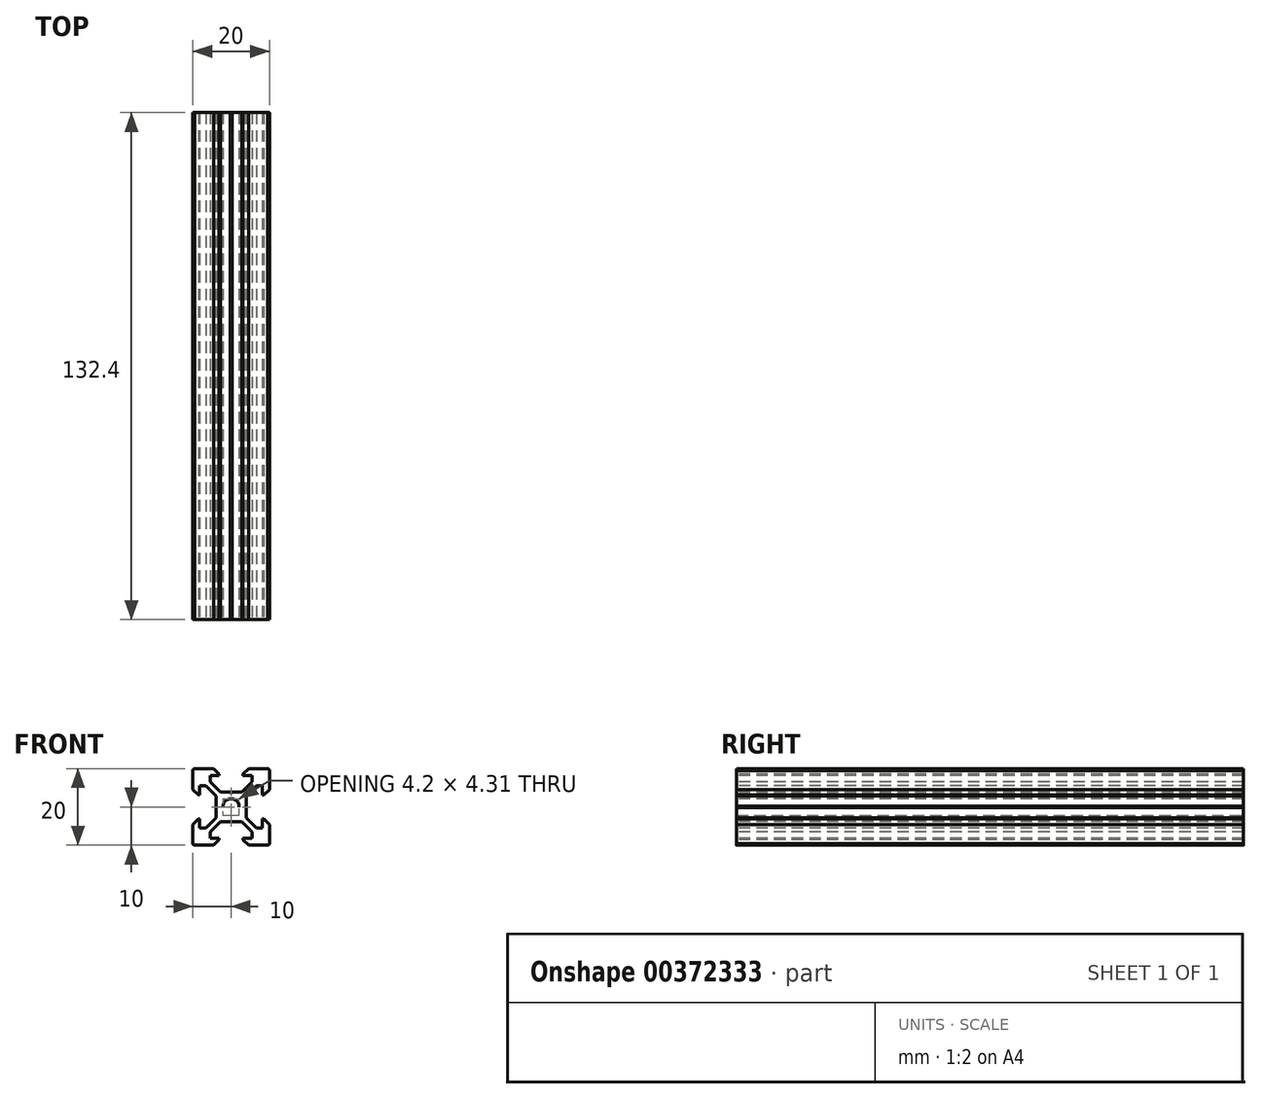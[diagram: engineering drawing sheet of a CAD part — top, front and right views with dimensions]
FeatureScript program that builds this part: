
annotation { "Feature Type Name" : "Feature", "Feature Type Description" : "" }
export const myFeature = defineFeature(function(context is Context, id is Id, definition is map)
    precondition{}
    {
        {
            var Q0;
            Q0=qCreatedBy(makeId("Front.planeOp"),FACE);
            var sketch = newSketch(context, id + "F0", { "sketchPlane" : qUnion([Q0])});
            skFitSpline(sketch, "E0.0", {"points": [v(-8.2, 3.13) * mm, v(-8.2, 3.92) * mm, v(-8.2, 4.7) * mm, v(-8.2, 5.5) * mm]});
            skFitSpline(sketch, "E0.1", {"points": [v(-8.2, 5.5) * mm, v(-7.65, 5.5) * mm, v(-7.1, 5.5) * mm, v(-6.56, 5.5) * mm]});
            skFitSpline(sketch, "E0.2", {"points": [v(-6.56, 5.5) * mm, v(-5.67, 4.61) * mm, v(-4.79, 3.73) * mm, v(-3.9, 2.84) * mm]});
            skFitSpline(sketch, "E0.3", {"points": [v(-2.84, 3.9) * mm, v(-3.73, 4.79) * mm, v(-4.61, 5.67) * mm, v(-5.5, 6.56) * mm]});
            skFitSpline(sketch, "E0.4", {"points": [v(-5.5, 6.56) * mm, v(-5.5, 7.1) * mm, v(-5.5, 7.65) * mm, v(-5.5, 8.2) * mm]});
            skFitSpline(sketch, "E0.5", {"points": [v(-5.5, 8.2) * mm, v(-4.7, 8.2) * mm, v(-3.92, 8.2) * mm, v(-3.12, 8.2) * mm]});
            skFitSpline(sketch, "E0.6", {"points": [v(-3.12, 8.2) * mm, v(-3.12, 8.32) * mm, v(-3.12, 8.43) * mm, v(-3.12, 8.55) * mm]});
            skFitSpline(sketch, "E0.7", {"points": [v(-10, 4.58) * mm, v(-9.51, 4.1) * mm, v(-9.03, 3.61) * mm, v(-8.54, 3.13) * mm]});
            skFitSpline(sketch, "E0.8", {"points": [v(-8.54, 3.13) * mm, v(-8.43, 3.13) * mm, v(-8.31, 3.13) * mm, v(-8.2, 3.13) * mm]});
            skFitSpline(sketch, "E0.9", {"points": [v(-10, 9.5) * mm, v(-10, 7.86) * mm, v(-10, 6.22) * mm, v(-10, 4.58) * mm]});
            skFitSpline(sketch, "E0.10", {"points": [v(-9.5, 10) * mm, v(-9.57, 10) * mm, v(-9.63, 9.99) * mm, v(-9.7, 9.96) * mm, v(-9.75, 9.94) * mm, v(-9.8, 9.9) * mm, v(-9.85, 9.85) * mm, v(-9.9, 9.8) * mm, v(-9.94, 9.75) * mm, v(-9.96, 9.7) * mm, v(-9.99, 9.63) * mm, v(-10, 9.57) * mm, v(-10, 9.5) * mm]});
            skFitSpline(sketch, "E0.11", {"points": [v(-4.58, 10) * mm, v(-6.22, 10) * mm, v(-7.86, 10) * mm, v(-9.5, 10) * mm]});
            skFitSpline(sketch, "E0.12", {"points": [v(-3.9, 2.84) * mm, v(-3.9, 1.96) * mm, v(-3.9, 1.09) * mm, v(-3.9, 0.21) * mm]});
            skFitSpline(sketch, "E0.13", {"points": [v(-3.9, 0.21) * mm, v(-3.83, 0.14) * mm, v(-3.76, 0.07) * mm, v(-3.69, 0) * mm]});
            skFitSpline(sketch, "E0.14", {"points": [v(-0.2, 3.9) * mm, v(-1.09, 3.9) * mm, v(-1.96, 3.9) * mm, v(-2.84, 3.9) * mm]});
            skFitSpline(sketch, "E0.15", {"points": [v(0, 3.7) * mm, v(-0.07, 3.76) * mm, v(-0.14, 3.83) * mm, v(-0.2, 3.9) * mm]});
            skFitSpline(sketch, "E0.16", {"points": [v(2.1, 0) * mm, v(2.1, 0.27) * mm, v(2, 0.82) * mm, v(1.52, 1.52) * mm, v(0.82, 2) * mm, v(0, 2.15) * mm, v(-0.82, 2) * mm, v(-1.52, 1.52) * mm, v(-2, 0.82) * mm, v(-2.1, 0.27) * mm, v(-2.1, 0) * mm]});
            skFitSpline(sketch, "E1.0", {"points": [v(-8.2, 3.13) * mm, v(-8.2, 3.92) * mm, v(-8.2, 4.7) * mm, v(-8.2, 5.5) * mm]});
            skFitSpline(sketch, "E1.1", {"points": [v(-8.2, 5.5) * mm, v(-7.65, 5.5) * mm, v(-7.1, 5.5) * mm, v(-6.56, 5.5) * mm]});
            skFitSpline(sketch, "E1.2", {"points": [v(-6.56, 5.5) * mm, v(-5.67, 4.61) * mm, v(-4.79, 3.73) * mm, v(-3.9, 2.84) * mm]});
            skFitSpline(sketch, "E1.3", {"points": [v(-2.84, 3.9) * mm, v(-3.73, 4.79) * mm, v(-4.61, 5.67) * mm, v(-5.5, 6.56) * mm]});
            skFitSpline(sketch, "E1.4", {"points": [v(-5.5, 6.56) * mm, v(-5.5, 7.1) * mm, v(-5.5, 7.65) * mm, v(-5.5, 8.2) * mm]});
            skFitSpline(sketch, "E1.5", {"points": [v(-5.5, 8.2) * mm, v(-4.7, 8.2) * mm, v(-3.92, 8.2) * mm, v(-3.12, 8.2) * mm]});
            skFitSpline(sketch, "E1.6", {"points": [v(-3.12, 8.2) * mm, v(-3.12, 8.32) * mm, v(-3.12, 8.43) * mm, v(-3.12, 8.55) * mm]});
            skFitSpline(sketch, "E1.7", {"points": [v(-10, 4.58) * mm, v(-9.51, 4.1) * mm, v(-9.03, 3.61) * mm, v(-8.54, 3.13) * mm]});
            skFitSpline(sketch, "E1.8", {"points": [v(-8.54, 3.13) * mm, v(-8.43, 3.13) * mm, v(-8.31, 3.13) * mm, v(-8.2, 3.13) * mm]});
            skFitSpline(sketch, "E1.9", {"points": [v(-10, 9.5) * mm, v(-10, 7.86) * mm, v(-10, 6.22) * mm, v(-10, 4.58) * mm]});
            skFitSpline(sketch, "E1.10", {"points": [v(-9.5, 10) * mm, v(-9.57, 10) * mm, v(-9.63, 9.99) * mm, v(-9.7, 9.96) * mm, v(-9.75, 9.94) * mm, v(-9.8, 9.9) * mm, v(-9.85, 9.85) * mm, v(-9.9, 9.8) * mm, v(-9.94, 9.75) * mm, v(-9.96, 9.7) * mm, v(-9.99, 9.63) * mm, v(-10, 9.57) * mm, v(-10, 9.5) * mm]});
            skFitSpline(sketch, "E1.11", {"points": [v(-4.58, 10) * mm, v(-6.22, 10) * mm, v(-7.86, 10) * mm, v(-9.5, 10) * mm]});
            skFitSpline(sketch, "E1.12", {"points": [v(-3.9, 2.84) * mm, v(-3.9, 1.96) * mm, v(-3.9, 1.09) * mm, v(-3.9, 0.21) * mm]});
            skFitSpline(sketch, "E1.13", {"points": [v(-3.9, 0.21) * mm, v(-3.83, 0.14) * mm, v(-3.76, 0.07) * mm, v(-3.69, 0) * mm]});
            skFitSpline(sketch, "E1.14", {"points": [v(-0.2, 3.9) * mm, v(-1.09, 3.9) * mm, v(-1.96, 3.9) * mm, v(-2.84, 3.9) * mm]});
            skFitSpline(sketch, "E1.15", {"points": [v(0, 3.7) * mm, v(-0.07, 3.76) * mm, v(-0.14, 3.83) * mm, v(-0.2, 3.9) * mm]});
            skFitSpline(sketch, "E1.16", {"points": [v(2.1, 0) * mm, v(2.1, 0.27) * mm, v(2, 0.82) * mm, v(1.52, 1.52) * mm, v(0.82, 2) * mm, v(0, 2.15) * mm, v(-0.82, 2) * mm, v(-1.52, 1.52) * mm, v(-2, 0.82) * mm, v(-2.1, 0.27) * mm, v(-2.1, 0) * mm]});
            skFitSpline(sketch, "E2.0", {"points": [v(2.84, 3.9) * mm, v(1.96, 3.9) * mm, v(1.09, 3.9) * mm, v(0.21, 3.9) * mm]});
            skFitSpline(sketch, "E2.1", {"points": [v(0.21, 3.9) * mm, v(0.14, 3.83) * mm, v(0.07, 3.76) * mm, v(0, 3.7) * mm]});
            skFitSpline(sketch, "E2.2", {"points": [v(3.9, 0.2) * mm, v(3.9, 1.09) * mm, v(3.9, 1.96) * mm, v(3.9, 2.84) * mm]});
            skFitSpline(sketch, "E2.3", {"points": [v(3.69, 0) * mm, v(3.76, 0.07) * mm, v(3.83, 0.14) * mm, v(3.9, 0.2) * mm]});
            skFitSpline(sketch, "E2.4", {"points": [v(3.9, 2.84) * mm, v(4.79, 3.73) * mm, v(5.67, 4.61) * mm, v(6.56, 5.5) * mm]});
            skFitSpline(sketch, "E2.5", {"points": [v(5.5, 6.56) * mm, v(4.61, 5.67) * mm, v(3.73, 4.79) * mm, v(2.84, 3.9) * mm]});
            skFitSpline(sketch, "E2.6", {"points": [v(6.56, 5.5) * mm, v(7.1, 5.5) * mm, v(7.65, 5.5) * mm, v(8.2, 5.5) * mm]});
            skFitSpline(sketch, "E2.7", {"points": [v(8.2, 5.5) * mm, v(8.2, 4.7) * mm, v(8.2, 3.92) * mm, v(8.2, 3.13) * mm]});
            skFitSpline(sketch, "E2.8", {"points": [v(8.2, 3.13) * mm, v(8.31, 3.13) * mm, v(8.43, 3.13) * mm, v(8.54, 3.13) * mm]});
            skFitSpline(sketch, "E2.9", {"points": [v(8.54, 3.13) * mm, v(9.03, 3.61) * mm, v(9.51, 4.1) * mm, v(10, 4.58) * mm]});
            skFitSpline(sketch, "E2.10", {"points": [v(10, 4.58) * mm, v(10, 6.22) * mm, v(10, 7.86) * mm, v(10, 9.5) * mm]});
            skFitSpline(sketch, "E2.11", {"points": [v(5.5, 8.2) * mm, v(5.5, 7.65) * mm, v(5.5, 7.1) * mm, v(5.5, 6.56) * mm]});
            skFitSpline(sketch, "E2.12", {"points": [v(3.13, 8.2) * mm, v(3.92, 8.2) * mm, v(4.7, 8.2) * mm, v(5.5, 8.2) * mm]});
            skFitSpline(sketch, "E2.13", {"points": [v(3.13, 8.55) * mm, v(3.13, 8.43) * mm, v(3.13, 8.32) * mm, v(3.13, 8.2) * mm]});
            skFitSpline(sketch, "E2.14", {"points": [v(9.5, 10) * mm, v(7.86, 10) * mm, v(6.22, 10) * mm, v(4.58, 10) * mm]});
            skFitSpline(sketch, "E2.15", {"points": [v(10, 9.5) * mm, v(10, 9.57) * mm, v(9.99, 9.63) * mm, v(9.96, 9.7) * mm, v(9.94, 9.75) * mm, v(9.9, 9.8) * mm, v(9.85, 9.85) * mm, v(9.8, 9.9) * mm, v(9.75, 9.94) * mm, v(9.7, 9.96) * mm, v(9.63, 9.99) * mm, v(9.57, 10) * mm, v(9.5, 10) * mm]});
            skFitSpline(sketch, "E2.16", {"points": [v(4.58, 10) * mm, v(4.1, 9.52) * mm, v(3.61, 9.03) * mm, v(3.13, 8.55) * mm]});
            skLineSegment(sketch, "E3", {"start": v(-4.58, 10) * mm, "end": v(-3.12, 8.55) * mm});
            skFitSpline(sketch, "E4.MirrorCS", {"points": [v(-3.9, -0.2) * mm, v(-3.83, -0.14) * mm, v(-3.76, -0.07) * mm, v(-3.69, 0) * mm]});
            skFitSpline(sketch, "E5.MirrorCS", {"points": [v(0, -3.7) * mm, v(-0.07, -3.76) * mm, v(-0.14, -3.83) * mm, v(-0.21, -3.9) * mm]});
            skFitSpline(sketch, "E6.MirrorCS", {"points": [v(-8.55, -3.12) * mm, v(-8.43, -3.12) * mm, v(-8.32, -3.12) * mm, v(-8.2, -3.12) * mm]});
            skFitSpline(sketch, "E7.MirrorCS", {"points": [v(0.2, -3.9) * mm, v(0.14, -3.83) * mm, v(0.07, -3.76) * mm, v(0, -3.7) * mm]});
            skFitSpline(sketch, "E8.MirrorCS", {"points": [v(-3.13, -8.2) * mm, v(-3.13, -8.31) * mm, v(-3.13, -8.43) * mm, v(-3.13, -8.54) * mm]});
            skFitSpline(sketch, "E9.MirrorCS", {"points": [v(-3.9, -0.2) * mm, v(-3.83, -0.14) * mm, v(-3.76, -0.07) * mm, v(-3.69, 0) * mm]});
            skFitSpline(sketch, "E10.MirrorCS", {"points": [v(-8.55, -3.12) * mm, v(-8.43, -3.12) * mm, v(-8.32, -3.12) * mm, v(-8.2, -3.12) * mm]});
            skFitSpline(sketch, "E11.MirrorCS", {"points": [v(0, -3.7) * mm, v(-0.07, -3.76) * mm, v(-0.14, -3.83) * mm, v(-0.21, -3.9) * mm]});
            skFitSpline(sketch, "E12.MirrorCS", {"points": [v(-3.13, -8.2) * mm, v(-3.13, -8.31) * mm, v(-3.13, -8.43) * mm, v(-3.13, -8.54) * mm]});
            skFitSpline(sketch, "E13.MirrorCS", {"points": [v(3.12, -8.55) * mm, v(3.12, -8.43) * mm, v(3.12, -8.32) * mm, v(3.12, -8.2) * mm]});
            skFitSpline(sketch, "E14.MirrorCS", {"points": [v(3.69, 0) * mm, v(3.76, -0.07) * mm, v(3.83, -0.14) * mm, v(3.9, -0.21) * mm]});
            skFitSpline(sketch, "E15.MirrorCS", {"points": [v(8.2, -3.13) * mm, v(8.31, -3.13) * mm, v(8.43, -3.13) * mm, v(8.54, -3.13) * mm]});
            skFitSpline(sketch, "E16.MirrorCS", {"points": [v(-8.2, -5.5) * mm, v(-7.65, -5.5) * mm, v(-7.1, -5.5) * mm, v(-6.56, -5.5) * mm]});
            skFitSpline(sketch, "E17.MirrorCS", {"points": [v(-2.84, -3.9) * mm, v(-3.73, -4.79) * mm, v(-4.61, -5.67) * mm, v(-5.5, -6.56) * mm]});
            skFitSpline(sketch, "E18.MirrorCS", {"points": [v(-5.5, -8.2) * mm, v(-4.7, -8.2) * mm, v(-3.92, -8.2) * mm, v(-3.13, -8.2) * mm]});
            skFitSpline(sketch, "E19.MirrorCS", {"points": [v(-5.5, -6.56) * mm, v(-5.5, -7.1) * mm, v(-5.5, -7.65) * mm, v(-5.5, -8.2) * mm]});
            skFitSpline(sketch, "E20.MirrorCS", {"points": [v(-0.21, -3.9) * mm, v(-1.09, -3.9) * mm, v(-1.96, -3.9) * mm, v(-2.84, -3.9) * mm]});
            skFitSpline(sketch, "E21.MirrorCS", {"points": [v(-8.2, -3.12) * mm, v(-8.2, -3.92) * mm, v(-8.2, -4.7) * mm, v(-8.2, -5.5) * mm]});
            skFitSpline(sketch, "E22.MirrorCS", {"points": [v(-10, -4.58) * mm, v(-9.52, -4.1) * mm, v(-9.03, -3.6) * mm, v(-8.55, -3.12) * mm]});
            skFitSpline(sketch, "E23.MirrorCS", {"points": [v(-10, -9.5) * mm, v(-10, -7.86) * mm, v(-10, -6.22) * mm, v(-10, -4.58) * mm]});
            skFitSpline(sketch, "E24.MirrorCS", {"points": [v(-9.5, -10) * mm, v(-9.57, -10) * mm, v(-9.63, -9.99) * mm, v(-9.7, -9.96) * mm, v(-9.75, -9.94) * mm, v(-9.8, -9.9) * mm, v(-9.85, -9.85) * mm, v(-9.9, -9.8) * mm, v(-9.94, -9.75) * mm, v(-9.96, -9.7) * mm, v(-9.99, -9.63) * mm, v(-10, -9.57) * mm, v(-10, -9.5) * mm]});
            skFitSpline(sketch, "E25.MirrorCS", {"points": [v(-4.58, -10) * mm, v(-6.22, -10) * mm, v(-7.86, -10) * mm, v(-9.5, -10) * mm]});
            skFitSpline(sketch, "E26.MirrorCS", {"points": [v(-3.9, -2.84) * mm, v(-3.9, -1.96) * mm, v(-3.9, -1.09) * mm, v(-3.9, -0.21) * mm]});
            skFitSpline(sketch, "E27.MirrorCS", {"points": [v(-6.56, -5.5) * mm, v(-5.67, -4.61) * mm, v(-4.79, -3.73) * mm, v(-3.9, -2.84) * mm]});
            skFitSpline(sketch, "E28.MirrorCS", {"points": [v(2.1, 0) * mm, v(2.1, -0.27) * mm, v(2, -0.82) * mm, v(1.52, -1.52) * mm, v(0.82, -2) * mm, v(0, -2.15) * mm, v(-0.82, -2) * mm, v(-1.52, -1.52) * mm, v(-2, -0.82) * mm, v(-2.1, -0.27) * mm, v(-2.1, 0) * mm]});
            skFitSpline(sketch, "E29.MirrorCS", {"points": [v(4.58, -10) * mm, v(4.1, -9.52) * mm, v(3.6, -9.03) * mm, v(3.12, -8.55) * mm]});
            skFitSpline(sketch, "E30.MirrorCS", {"points": [v(-6.56, -5.5) * mm, v(-5.67, -4.61) * mm, v(-4.79, -3.73) * mm, v(-3.9, -2.84) * mm]});
            skFitSpline(sketch, "E31.MirrorCS", {"points": [v(10, -4.58) * mm, v(10, -6.22) * mm, v(10, -7.86) * mm, v(10, -9.5) * mm]});
            skLineSegment(sketch, "E32.MirrorCS", {"start": v(-4.58, -10) * mm, "end": v(-3.13, -8.54) * mm});
            skFitSpline(sketch, "E33.MirrorCS", {"points": [v(-4.58, -10) * mm, v(-6.22, -10) * mm, v(-7.86, -10) * mm, v(-9.5, -10) * mm]});
            skFitSpline(sketch, "E34.MirrorCS", {"points": [v(6.56, -5.5) * mm, v(7.1, -5.5) * mm, v(7.65, -5.5) * mm, v(8.2, -5.5) * mm]});
            skFitSpline(sketch, "E35.MirrorCS", {"points": [v(-10, -4.58) * mm, v(-9.52, -4.1) * mm, v(-9.03, -3.6) * mm, v(-8.55, -3.12) * mm]});
            skFitSpline(sketch, "E36.MirrorCS", {"points": [v(-5.5, -6.56) * mm, v(-5.5, -7.1) * mm, v(-5.5, -7.65) * mm, v(-5.5, -8.2) * mm]});
            skFitSpline(sketch, "E37.MirrorCS", {"points": [v(3.12, -8.2) * mm, v(3.92, -8.2) * mm, v(4.7, -8.2) * mm, v(5.5, -8.2) * mm]});
            skFitSpline(sketch, "E38.MirrorCS", {"points": [v(-8.2, -5.5) * mm, v(-7.65, -5.5) * mm, v(-7.1, -5.5) * mm, v(-6.56, -5.5) * mm]});
            skFitSpline(sketch, "E39.MirrorCS", {"points": [v(-8.2, -3.12) * mm, v(-8.2, -3.92) * mm, v(-8.2, -4.7) * mm, v(-8.2, -5.5) * mm]});
            skFitSpline(sketch, "E40.MirrorCS", {"points": [v(10, -9.5) * mm, v(10, -9.57) * mm, v(9.99, -9.63) * mm, v(9.96, -9.7) * mm, v(9.94, -9.75) * mm, v(9.9, -9.8) * mm, v(9.85, -9.85) * mm, v(9.8, -9.9) * mm, v(9.75, -9.94) * mm, v(9.7, -9.96) * mm, v(9.63, -9.99) * mm, v(9.57, -10) * mm, v(9.5, -10) * mm]});
            skFitSpline(sketch, "E41.MirrorCS", {"points": [v(2.1, 0) * mm, v(2.1, -0.27) * mm, v(2, -0.82) * mm, v(1.52, -1.52) * mm, v(0.82, -2) * mm, v(0, -2.15) * mm, v(-0.82, -2) * mm, v(-1.52, -1.52) * mm, v(-2, -0.82) * mm, v(-2.1, -0.27) * mm, v(-2.1, 0) * mm]});
            skFitSpline(sketch, "E42.MirrorCS", {"points": [v(2.84, -3.9) * mm, v(1.96, -3.9) * mm, v(1.09, -3.9) * mm, v(0.2, -3.9) * mm]});
            skFitSpline(sketch, "E43.MirrorCS", {"points": [v(-10, -9.5) * mm, v(-10, -7.86) * mm, v(-10, -6.22) * mm, v(-10, -4.58) * mm]});
            skFitSpline(sketch, "E44.MirrorCS", {"points": [v(8.2, -5.5) * mm, v(8.2, -4.7) * mm, v(8.2, -3.92) * mm, v(8.2, -3.13) * mm]});
            skFitSpline(sketch, "E45.MirrorCS", {"points": [v(8.54, -3.13) * mm, v(9.03, -3.61) * mm, v(9.51, -4.1) * mm, v(10, -4.58) * mm]});
            skFitSpline(sketch, "E46.MirrorCS", {"points": [v(3.9, -2.84) * mm, v(4.79, -3.73) * mm, v(5.67, -4.61) * mm, v(6.56, -5.5) * mm]});
            skFitSpline(sketch, "E47.MirrorCS", {"points": [v(-9.5, -10) * mm, v(-9.57, -10) * mm, v(-9.63, -9.99) * mm, v(-9.7, -9.96) * mm, v(-9.75, -9.94) * mm, v(-9.8, -9.9) * mm, v(-9.85, -9.85) * mm, v(-9.9, -9.8) * mm, v(-9.94, -9.75) * mm, v(-9.96, -9.7) * mm, v(-9.99, -9.63) * mm, v(-10, -9.57) * mm, v(-10, -9.5) * mm]});
            skFitSpline(sketch, "E48.MirrorCS", {"points": [v(-0.21, -3.9) * mm, v(-1.09, -3.9) * mm, v(-1.96, -3.9) * mm, v(-2.84, -3.9) * mm]});
            skFitSpline(sketch, "E49.MirrorCS", {"points": [v(5.5, -6.56) * mm, v(4.61, -5.67) * mm, v(3.73, -4.79) * mm, v(2.84, -3.9) * mm]});
            skFitSpline(sketch, "E50.MirrorCS", {"points": [v(-2.84, -3.9) * mm, v(-3.73, -4.79) * mm, v(-4.61, -5.67) * mm, v(-5.5, -6.56) * mm]});
            skFitSpline(sketch, "E51.MirrorCS", {"points": [v(-5.5, -8.2) * mm, v(-4.7, -8.2) * mm, v(-3.92, -8.2) * mm, v(-3.13, -8.2) * mm]});
            skFitSpline(sketch, "E52.MirrorCS", {"points": [v(5.5, -8.2) * mm, v(5.5, -7.65) * mm, v(5.5, -7.1) * mm, v(5.5, -6.56) * mm]});
            skFitSpline(sketch, "E53.MirrorCS", {"points": [v(3.9, -0.21) * mm, v(3.9, -1.09) * mm, v(3.9, -1.96) * mm, v(3.9, -2.84) * mm]});
            skFitSpline(sketch, "E54.MirrorCS", {"points": [v(-3.9, -2.84) * mm, v(-3.9, -1.96) * mm, v(-3.9, -1.09) * mm, v(-3.9, -0.21) * mm]});
            skFitSpline(sketch, "E55.MirrorCS", {"points": [v(9.5, -10) * mm, v(7.86, -10) * mm, v(6.22, -10) * mm, v(4.58, -10) * mm]});
            skLineSegment(sketch, "E56.MirrorCS", {"start": v(0, 3.7) * mm, "end": v(0, 0) * mm, "construction": true});
            skLineSegment(sketch, "E57.MirrorCS", {"start": v(0, -3.7) * mm, "end": v(0, 0) * mm, "construction": true});
            skSolve(sketch);
        }
        {
            var Q0;
            Q0=qSketchRegion(id+"F0",true);
            extrude(context, id + "F1", {"entities" : qUnion([Q0]), "oppositeDirection" : true, "depth" : 152.4 * mm - 20 * mm});
        }
    });
